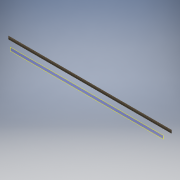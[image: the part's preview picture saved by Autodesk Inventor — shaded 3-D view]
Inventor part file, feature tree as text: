
AUTODESK INVENTOR PART (.ipt)
format: ipt  version: 2017 (Build 210142000, 142)  size: 133,632 bytes
history: native  units: mm
features: extrude x2, chamfer x2, sketch x2, plane x1, projected_geometry x1
ambient origin geometry x8: Origin, YZ Plane, XZ Plane, XY Plane, X Axis, Y Axis, Z Axis, Center Point
bodies: Volumenkörper1 (feature_tree)
feature tree (8):
  plane  "Arbeitsebene1"
  extrude  "Extrusion1"  Depth=100.0mm
  extrude  "Extrusion2"  Depth=5.0mm
  chamfer  "Fase1"  Distance=11.0mm
  chamfer  "Fase2"  Distance=4.0mm
  sketch  "Skizze1"  dims[d0=4680.0mm d1=100.0mm]
  sketch  "Skizze2"  dims[d2=15.0mm d3=0.0mm d4=5.0mm d5=11.0mm d6=4.0mm d7=10.0mm d8=15.0mm d9=0.0mm d10=2.0mm d11=2.0mm d12=45.0deg d13=1.0mm d14=2.0mm d15=45.0deg]
  projected_geometry  "Projizierte Kontur1"
